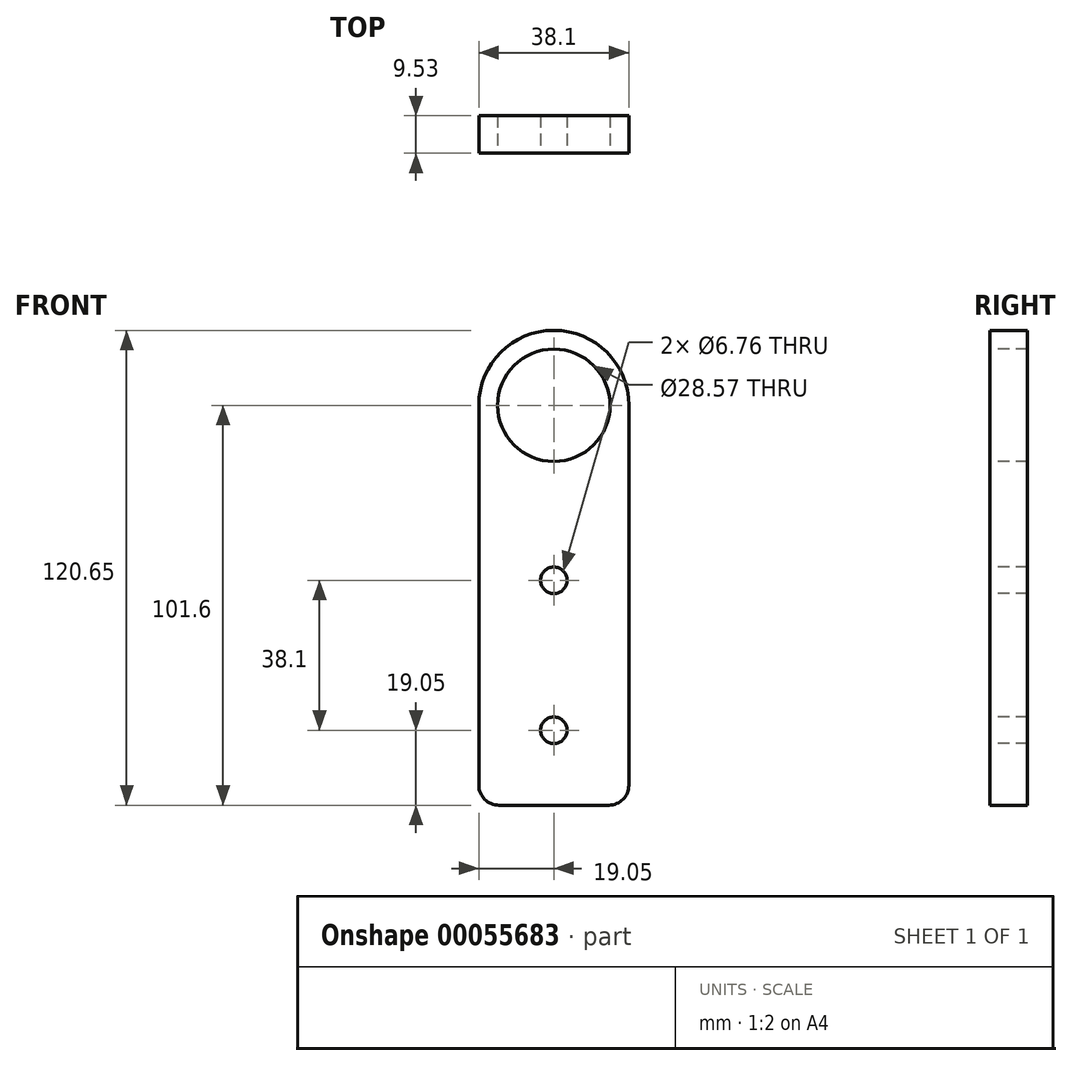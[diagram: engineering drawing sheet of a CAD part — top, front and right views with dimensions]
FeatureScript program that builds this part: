
annotation { "Feature Type Name" : "Feature", "Feature Type Description" : "" }
export const myFeature = defineFeature(function(context is Context, id is Id, definition is map)
    precondition{}
    {
        {
            var Q0;
            Q0=qCreatedBy(makeId("Front.planeOp"),FACE);
            var sketch = newSketch(context, id + "F0", { "sketchPlane" : qUnion([Q0])});
            skLineSegment(sketch, "E0.bottom", {"start": v(0, 0) * mm, "end": v(38.1, 0) * mm});
            skLineSegment(sketch, "E0.top", {"start": v(0, 101.6) * mm, "end": v(38.1, 101.6) * mm});
            skLineSegment(sketch, "E0.left", {"start": v(0, 0) * mm, "end": v(0, 101.6) * mm});
            skLineSegment(sketch, "E0.right", {"start": v(38.1, 0) * mm, "end": v(38.1, 101.6) * mm});
            skArc(sketch, "E1", {"start": v(38.1, 101.6) * mm, "mid": v(19.05, 120.65) * mm, "end": v(0, 101.6) * mm});
            skCircle(sketch, "E2", {"center": v(19.05, 101.6) * mm, "radius": 14.29 * mm});
            skLineSegment(sketch, "E3", {"start": v(19.05, 101.6) * mm, "end": v(19.05, 0) * mm});
            skCircle(sketch, "E4", {"center": v(19.05, 57.15) * mm, "radius": 3.38 * mm});
            skCircle(sketch, "E5", {"center": v(19.05, 19.05) * mm, "radius": 3.38 * mm});
            skSolve(sketch);
        }
        {
            var Q0;
            Q0 = qSketchRegion(id + "F0", true);
            extrude(context, id + "F1", {"entities" : qUnion([Q0]), "oppositeDirection" : true, "depth" : 9.52 * mm});
        }
        {
            var Q0;
            Q0=makeQuery(id+"F1.opExtrude","SWEPT_FACE",FACE,{"disambiguationData":[OSD([sQuery(id+"F0.wireOp",EDGE,"E0.right")])]});
            var sketch = newSketch(context, id + "F2", { "sketchPlane" : qUnion([Q0])});
            skLineSegment(sketch, "E6", {"start": v(4.76, 101.6) * mm, "end": v(4.76, 0) * mm});
            skPoint(sketch, "E7", {"position": v(4.76, 57.15) * mm});
            skSolve(sketch);
        }
        {
            var Q0;
            Q0=makeQuery(id+"F1.opExtrude","SWEPT_EDGE",EDGE,{"disambiguationData":[OSD([sQuery(id+"F0.wireOp",EDGE,"E0.bottom"),sQuery(id+"F0.wireOp",EDGE,"E0.right")])]});
            var Q1;
            Q1=makeQuery(id+"F1.opExtrude","SWEPT_EDGE",EDGE,{"disambiguationData":[OSD([sQuery(id+"F0.wireOp",EDGE,"E0.bottom"),sQuery(id+"F0.wireOp",EDGE,"E0.left")])]});
            fillet(context, id + "F3", {"entities" : qUnion([Q0, Q1]), "radius" : 5.08 * mm, "tangentPropagation" : true, "allowEdgeOverflow" : false});
        }
    });
